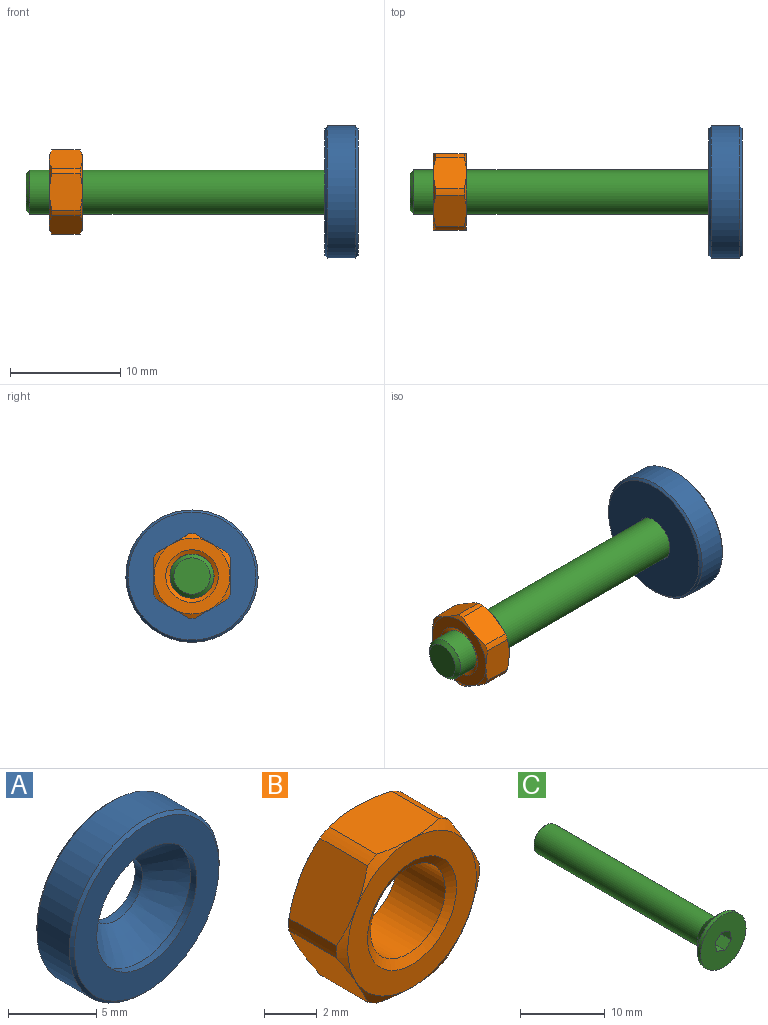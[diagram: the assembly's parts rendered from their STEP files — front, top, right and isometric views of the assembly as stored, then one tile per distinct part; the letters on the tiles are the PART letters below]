
ASSEMBLY  parts=3 mates=2
PART A: 8 faces, bbox 12x3x12 mm
  f0: cylinder r=2.08mm len=4.15mm, axis (0,1,0), area 7.5mm2, adj f3,f4
  f1: cylinder r=6mm len=12mm, axis (0,1,0), area 98mm2, adj f6,f7
  f2: plane 11.6x11.6mm, normal (0,-1,0), area 55.4mm2, adj f5,f7
  f3: plane 11.6x11.6mm, normal (0,1,0), area 92.2mm2, adj f0,f6
  f4: cone r=4mm half-angle=45deg, axis (0,-1,0), area 52mm2, adj f0,f5
  f5: cylinder r=4mm len=8mm, axis (0,-1,0), area 12.6mm2, adj f2,f4
  f6: cone r=6mm half-angle=45deg, axis (0,-1,0), area 10.5mm2, adj f1,f3
  f7: cone r=5.8mm half-angle=45deg, axis (0,1,0), area 10.5mm2, adj f1,f2
PART B: 19 faces, bbox 7.7x3x7.7 mm
  f0: cylinder r=3.83mm len=2.56mm, axis (0,-1,0), area 1.5mm2, adj f11,f12,f17,f18
  f1: cylinder r=3.83mm len=2.56mm, axis (0,-1,0), area 1.5mm2, adj f11,f12,f16,f17
  f2: cylinder r=3.83mm len=2.56mm, axis (0,-1,0), area 1.5mm2, adj f11,f12,f15,f16
  f3: cylinder r=3.83mm len=2.56mm, axis (0,-1,0), area 1.5mm2, adj f11,f12,f14,f15
  f4: cylinder r=3.83mm len=2.56mm, axis (0,-1,0), area 1.5mm2, adj f11,f12,f13,f14
  f5: cylinder r=2mm len=4mm, axis (0,-1,0), area 32.1mm2, adj f9,f10
  f6: plane 6.89x6.89mm, normal (0,1,0), area 19.4mm2, adj f9,f11
  f7: cylinder r=3.83mm len=2.56mm, axis (0,-1,0), area 1.5mm2, adj f11,f12,f13,f18
  f8: plane 6.89x6.89mm, normal (0,-1,0), area 19.4mm2, adj f10,f12
  f9: cone r=2.38mm half-angle=60deg, axis (0,1,0), area 6.1mm2, adj f5,f6
  f10: cone r=2mm half-angle=60deg, axis (0,-1,0), area 6.1mm2, adj f5,f8
  f11: cone r=3.83mm half-angle=60deg, axis (0,-1,0), area 4.3mm2, adj f0,f1,f2,f3,f4,f6,f7,f13
  f12: cone r=3.45mm half-angle=60deg, axis (0,1,0), area 4.3mm2, adj f0,f1,f2,f3,f4,f7,f8,f13
  f13: plane 3x2.88mm, normal (-0.87,0,0.5), area 9.5mm2, adj f4,f7,f11,f12
  f14: plane 3x2.88mm, normal (-0.87,0,-0.5), area 9.5mm2, adj f3,f4,f11,f12
  f15: plane 3.33x3mm, normal (0,0,-1), area 9.5mm2, adj f2,f3,f11,f12
  f16: plane 3x2.88mm, normal (0.87,0,-0.5), area 9.5mm2, adj f1,f2,f11,f12
  f17: plane 3x2.88mm, normal (0.87,0,0.5), area 9.5mm2, adj f0,f1,f11,f12
  f18: plane 3.33x3mm, normal (0,0,1), area 9.5mm2, adj f0,f7,f11,f12
PART C: 13 faces, bbox 7.6x30x7.6 mm
  f0: plane 7.6x7.6mm, normal (0,-1,0), area 40mm2, adj f5,f6,f7,f8,f9,f10,f11
  f1: plane 3.29x3.29mm, normal (0,1,0), area 8.5mm2, adj f2
  f2: cone r=2mm half-angle=45deg, axis (0,-1,0), area 5.7mm2, adj f1,f3
  f3: cylinder r=2mm len=27.35mm, axis (0,1,0), area 343.6mm2, adj f2,f4
  f4: cone r=3.8mm half-angle=45deg, axis (0,-1,0), area 46.4mm2, adj f3,f5
  f5: cylinder r=3.8mm len=7.6mm, axis (0,1,0), area 11.9mm2, adj f0,f4
  f6: plane 1.8x1.1mm, normal (0.65,0,-0.76), area 2.6mm2, adj f0,f7,f11,f12
  f7: plane 1.8x1.42mm, normal (0.98,0,0.18), area 2.6mm2, adj f0,f6,f8,f12
  f8: plane 1.8x1.36mm, normal (0.33,0,0.94), area 2.6mm2, adj f0,f7,f9,f12
  f9: plane 1.8x1.1mm, normal (-0.65,0,0.76), area 2.6mm2, adj f0,f8,f10,f12
  f10: plane 1.8x1.42mm, normal (-0.98,0,-0.18), area 2.6mm2, adj f0,f9,f11,f12
  f11: plane 1.8x1.36mm, normal (-0.33,0,-0.94), area 2.6mm2, adj f0,f6,f10,f12
  f12: plane 2.84x2.72mm, normal (0,-1,0), area 5.4mm2, adj f6,f7,f8,f9,f10,f11
PLACE A rot(axis=(0.71,-0.71,0),180deg) t=(7.15,24.48,86.05)mm
PLACE B rot(axis=(-0.58,0.58,0.58),120deg) t=(-17.35,39.15,98)mm
PLACE C rot(axis=(0.71,-0.71,0),180deg) t=(-3.9,132.15,98)mm
MATE fastened B.f0 <-> A.f0  axis (1,0,0) through (-17.35,39.15,98)mm
MATE fastened A.f0 <-> C.f2  axis (1,0,0) through (5.22,39.15,98)mm
